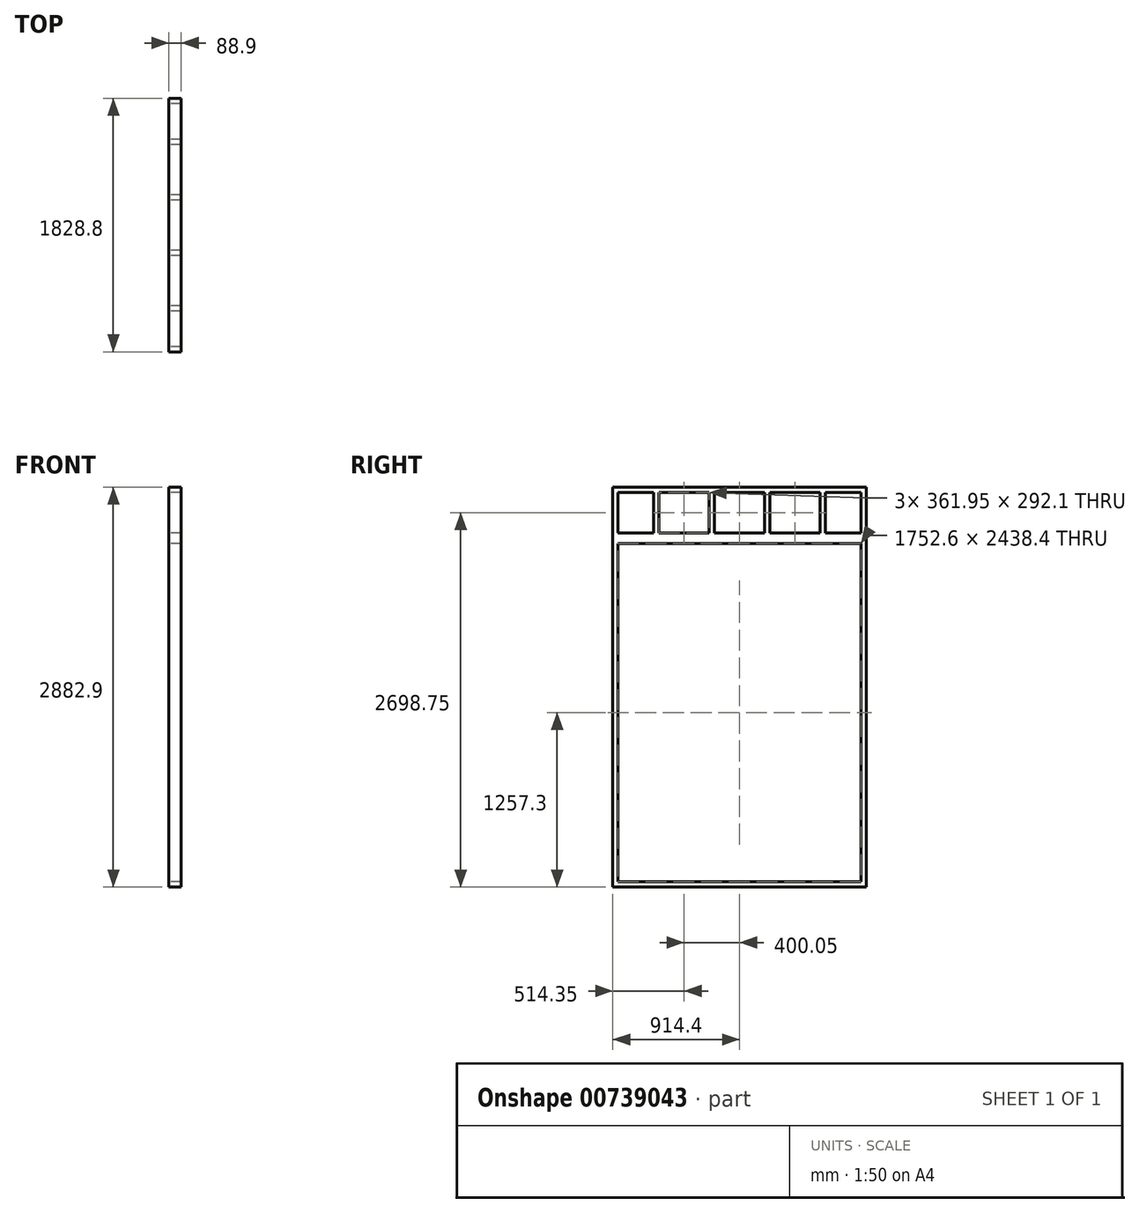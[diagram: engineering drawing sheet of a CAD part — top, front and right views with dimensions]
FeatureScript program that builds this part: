
annotation { "Feature Type Name" : "Feature", "Feature Type Description" : "" }
export const myFeature = defineFeature(function(context is Context, id is Id, definition is map)
    precondition{}
    {
        {
            var Q0;
            Q0=qCreatedBy(makeId("Right.planeOp"),FACE);
            var sketch = newSketch(context, id + "F0", { "sketchPlane" : qUnion([Q0])});
            skLineSegment(sketch, "E0.bottom", {"start": v(0, 0) * mm, "end": v(1828.8, 0) * mm});
            skLineSegment(sketch, "E0.top", {"start": v(0, 2476.5) * mm, "end": v(1828.8, 2476.5) * mm});
            skLineSegment(sketch, "E0.left", {"start": v(0, 0) * mm, "end": v(0, 2476.5) * mm});
            skLineSegment(sketch, "E0.right", {"start": v(1828.8, 0) * mm, "end": v(1828.8, 2476.5) * mm});
            skLineSegment(sketch, "E1.top", {"start": v(0, 2882.9) * mm, "end": v(1828.8, 2882.9) * mm});
            skLineSegment(sketch, "E1.left", {"start": v(0, 2476.5) * mm, "end": v(0, 2882.9) * mm});
            skLineSegment(sketch, "E1.right", {"start": v(1828.8, 2476.5) * mm, "end": v(1828.8, 2882.9) * mm});
            skLineSegment(sketch, "E2.0", {"start": v(0, 2844.8) * mm, "end": v(1828.8, 2844.8) * mm});
            skLineSegment(sketch, "E3.0", {"start": v(0, 38.1) * mm, "end": v(1828.8, 38.1) * mm});
            skLineSegment(sketch, "E4.0", {"start": v(0, 2514.6) * mm, "end": v(1828.8, 2514.6) * mm});
            skLineSegment(sketch, "E5.0", {"start": v(0, 2552.7) * mm, "end": v(1828.8, 2552.7) * mm});
            skLineSegment(sketch, "E6.1", {"start": v(38.1, 0) * mm, "end": v(38.1, 2476.5) * mm});
            skLineSegment(sketch, "E7.0", {"start": v(1790.7, 0) * mm, "end": v(1790.7, 2476.5) * mm});
            skLineSegment(sketch, "E8.bottom", {"start": v(295.27, 2476.5) * mm, "end": v(333.37, 2476.5) * mm});
            skLineSegment(sketch, "E8.top", {"start": v(295.27, 38.1) * mm, "end": v(333.37, 38.1) * mm});
            skLineSegment(sketch, "E8.left", {"start": v(295.27, 2476.5) * mm, "end": v(295.27, 38.1) * mm});
            skLineSegment(sketch, "E8.right", {"start": v(333.37, 2476.5) * mm, "end": v(333.37, 38.1) * mm});
            skLineSegment(sketch, "E9.bottom", {"start": v(1095.38, 2476.5) * mm, "end": v(1133.47, 2476.5) * mm});
            skLineSegment(sketch, "E9.top", {"start": v(1095.38, 38.1) * mm, "end": v(1133.47, 38.1) * mm});
            skLineSegment(sketch, "E9.left", {"start": v(1095.38, 2476.5) * mm, "end": v(1095.38, 38.1) * mm});
            skLineSegment(sketch, "E9.right", {"start": v(1133.47, 2476.5) * mm, "end": v(1133.47, 38.1) * mm});
            skLineSegment(sketch, "E10.bottom", {"start": v(695.32, 2476.5) * mm, "end": v(733.42, 2476.5) * mm});
            skLineSegment(sketch, "E10.top", {"start": v(695.33, 38.1) * mm, "end": v(733.43, 38.1) * mm});
            skLineSegment(sketch, "E10.left", {"start": v(695.32, 2476.5) * mm, "end": v(695.33, 38.1) * mm});
            skLineSegment(sketch, "E10.right", {"start": v(733.42, 2476.5) * mm, "end": v(733.43, 38.1) * mm});
            skLineSegment(sketch, "E11.bottom", {"start": v(1495.42, 2476.5) * mm, "end": v(1533.53, 2476.5) * mm});
            skLineSegment(sketch, "E11.top", {"start": v(1495.42, 38.1) * mm, "end": v(1533.53, 38.1) * mm});
            skLineSegment(sketch, "E11.left", {"start": v(1495.42, 2476.5) * mm, "end": v(1495.42, 38.1) * mm});
            skLineSegment(sketch, "E11.right", {"start": v(1533.53, 2476.5) * mm, "end": v(1533.53, 38.1) * mm});
            skLineSegment(sketch, "E12", {"start": v(1495.42, 2552.7) * mm, "end": v(1495.42, 2844.8) * mm});
            skLineSegment(sketch, "E13.trimOffspring", {"start": v(295.27, 2552.7) * mm, "end": v(295.27, 2844.8) * mm});
            skLineSegment(sketch, "E14.trimOffspring", {"start": v(333.37, 2552.7) * mm, "end": v(333.37, 2844.8) * mm});
            skLineSegment(sketch, "E15.trimOffspring", {"start": v(695.32, 2552.7) * mm, "end": v(695.32, 2844.8) * mm});
            skLineSegment(sketch, "E16.trimOffspring", {"start": v(733.42, 2552.7) * mm, "end": v(733.42, 2844.8) * mm});
            skLineSegment(sketch, "E17.trimOffspring", {"start": v(38.1, 2552.7) * mm, "end": v(38.1, 2844.8) * mm});
            skLineSegment(sketch, "E18.trimOffspring", {"start": v(1790.7, 2552.7) * mm, "end": v(1790.7, 2844.8) * mm});
            skLineSegment(sketch, "E19.trimOffspring", {"start": v(1533.53, 2552.7) * mm, "end": v(1533.53, 2844.8) * mm});
            skLineSegment(sketch, "E20.trimOffspring", {"start": v(1095.38, 2552.7) * mm, "end": v(1095.38, 2844.8) * mm});
            skLineSegment(sketch, "E21.trimOffspring", {"start": v(1133.47, 2552.7) * mm, "end": v(1133.47, 2844.8) * mm});
            skSolve(sketch);
        }
        {
            var Q0;
            Q0 = qSketchRegion(id + "F0", true);
            var Q1;
            Q1=makeQuery(id+"F0.imprint","IMPRINT",FACE,{"disambiguationData":[TD([[makeQuery(id+"F0.imprint","IMPRINT",EDGE,{"derivedFrom":sQuery(id+"F0.wireOp",EDGE,"E8.bottom")}),-1.0]])]});
            var Q2;
            Q2=makeQuery(id+"F0.imprint","IMPRINT",FACE,{"disambiguationData":[TD([[makeQuery(id+"F0.imprint","IMPRINT",EDGE,{"derivedFrom":sQuery(id+"F0.wireOp",EDGE,"E10.bottom")}),-1.0]])]});
            var Q3;
            Q3=makeQuery(id+"F0.imprint","IMPRINT",FACE,{"disambiguationData":[TD([[makeQuery(id+"F0.imprint","IMPRINT",EDGE,{"derivedFrom":sQuery(id+"F0.wireOp",EDGE,"E9.bottom")}),-1.0]])]});
            var Q4;
            Q4=makeQuery(id+"F0.imprint","IMPRINT",FACE,{"disambiguationData":[TD([[makeQuery(id+"F0.imprint","IMPRINT",EDGE,{"derivedFrom":sQuery(id+"F0.wireOp",EDGE,"E11.bottom")}),-1.0]])]});
            var Q5;
            {var subQ0=sQuery(id+"F0.wireOp",EDGE,"E12");Q5=makeQuery(id+"F0.imprint","IMPRINT",FACE,{"disambiguationData":[TD([[makeQuery(id+"F0.imprint","IMPRINT",EDGE,{"derivedFrom":subQ0}),-1.0]])]});}
            var Q6;
            {var subQ0=sQuery(id+"F0.wireOp",EDGE,"E20.trimOffspring");Q6=makeQuery(id+"F0.imprint","IMPRINT",FACE,{"disambiguationData":[TD([[makeQuery(id+"F0.imprint","IMPRINT",EDGE,{"derivedFrom":subQ0}),-1.0]])]});}
            var Q7;
            {var subQ0=sQuery(id+"F0.wireOp",EDGE,"E15.trimOffspring");Q7=makeQuery(id+"F0.imprint","IMPRINT",FACE,{"disambiguationData":[TD([[makeQuery(id+"F0.imprint","IMPRINT",EDGE,{"derivedFrom":subQ0}),-1.0]])]});}
            var Q8;
            {var subQ0=sQuery(id+"F0.wireOp",EDGE,"E13.trimOffspring");Q8=makeQuery(id+"F0.imprint","IMPRINT",FACE,{"disambiguationData":[TD([[makeQuery(id+"F0.imprint","IMPRINT",EDGE,{"derivedFrom":subQ0}),-1.0]])]});}
            extrude(context, id + "F1", {"entities" : qUnion([Q0, Q1, Q2, Q3, Q4, Q5, Q6, Q7, Q8]), "depth" : 88.9 * mm, "offsetDistance" : 25.4 * mm});
        }
    });
